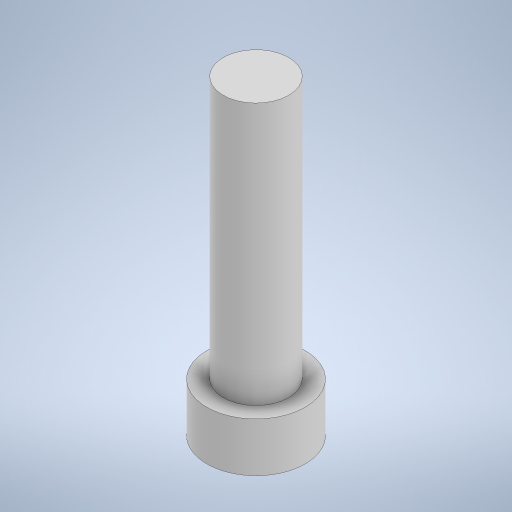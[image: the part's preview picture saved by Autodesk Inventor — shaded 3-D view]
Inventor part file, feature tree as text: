
AUTODESK INVENTOR PART (.ipt)
format: ipt  version: 2024.2 (Build 282272000, 272)  size: 235,520 bytes
history: native  units: mm
features: extrude x2, sketch x2
ambient origin geometry x8: Origin, YZ Plane, XZ Plane, XY Plane, X Axis, Y Axis, Z Axis, Center Point
bodies: Solid1 (feature_tree)
feature tree (4):
  extrude  "Extrusion1"  Depth=1.5mm TaperAngle=0.0deg
  extrude  "Extrusion2"  Depth=8.0mm TaperAngle=0.0deg
  sketch  "Sketch1"  dims[d0=3.0mm d1=1.5mm d2=0.0mm]
  sketch  "Sketch2"  dims[d3=2.0mm d4=8.0mm d5=0.0mm]
